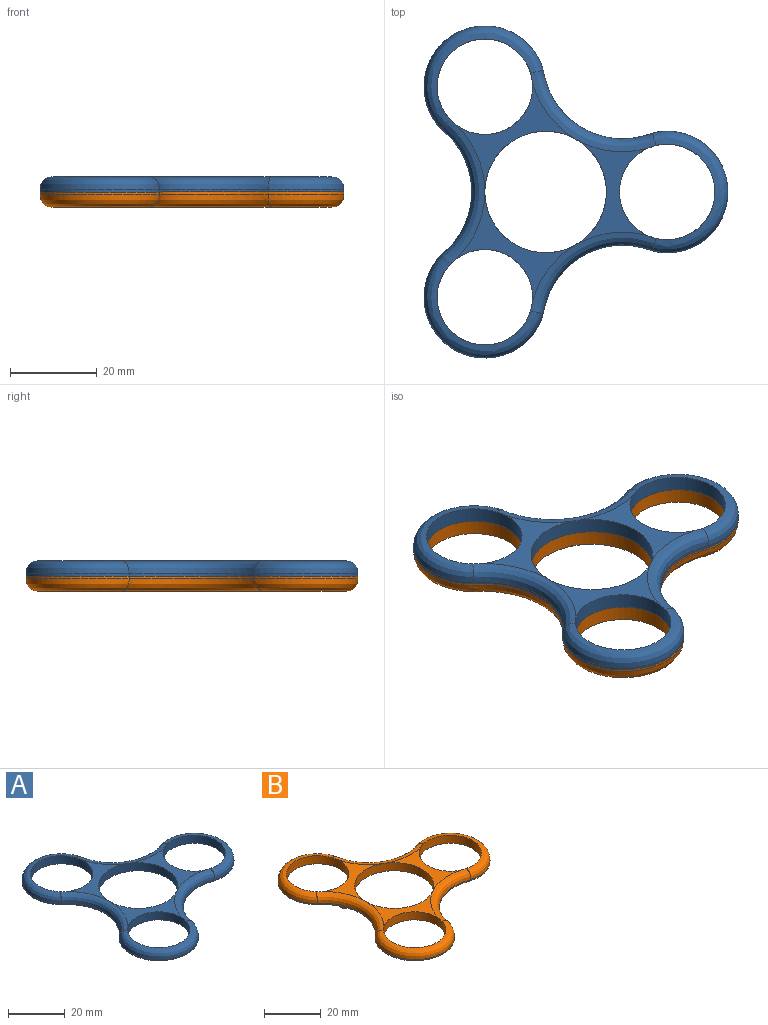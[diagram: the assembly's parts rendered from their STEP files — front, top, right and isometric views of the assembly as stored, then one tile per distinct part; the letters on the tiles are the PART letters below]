
ASSEMBLY  parts=2 mates=1
PART A: 32 faces, bbox 70.2x76.6x3.5 mm
  f0: plane 27.54x25.49mm, normal (0,0,1), area 113.9mm2, adj f7,f9,f16,f19
  f1: plane 24.28x16.61mm, normal (0,0,1), area 114mm2, adj f7,f10,f15,f19
  f2: cylinder r=18.43mm len=25.08mm, axis (0,0,-1), area 16.7mm2, adj f3,f11,f13,f15
  f3: cylinder r=14mm len=27.47mm, axis (0,0,-1), area 25.5mm2, adj f2,f4,f13,f14
  f4: cylinder r=18.43mm len=28.96mm, axis (0,0,-1), area 16.7mm2, adj f3,f5,f13,f16
  f5: cylinder r=14mm len=27.47mm, axis (0,0,-1), area 25.5mm2, adj f4,f6,f13,f18
  f6: cylinder r=18.43mm len=25.08mm, axis (0,0,-1), area 16.7mm2, adj f5,f11,f13,f19
  f7: cylinder r=14mm len=28mm, axis (0,0,-1), area 307.9mm2, adj f0,f1,f12,f13
  f8: cylinder r=11mm len=22mm, axis (0,0,-1), area 241.9mm2, adj f12,f13,f14,f15,f16
  f9: cylinder r=11mm len=22mm, axis (0,0,-1), area 241.9mm2, adj f0,f13,f16,f18,f19
  f10: cylinder r=11mm len=22mm, axis (0,0,-1), area 241.9mm2, adj f1,f13,f15,f17,f19
  f11: cylinder r=14mm len=28mm, axis (0,0,-1), area 25.5mm2, adj f2,f6,f13,f17
  f12: plane 27.54x25.49mm, normal (0,0,1), area 113.9mm2, adj f7,f8,f15,f16
  f13: plane 76.5x70mm, normal (0,0,-1), area 1029.2mm2, adj f2,f3,f4,f5,f6,f7,f8,f9
  f14: bspline ~27.47x23.76mm, area 228.9mm2, adj f3,f8,f15,f16
  f15: bspline ~31.12x20.64mm, area 170.3mm2, adj f1,f2,f8,f10,f12,f14,f17
  f16: bspline ~35.93x11.38mm, area 170.3mm2, adj f0,f4,f8,f9,f12,f14,f18
  f17: bspline ~27.99x17.43mm, area 228.9mm2, adj f10,f11,f15,f19
  f18: bspline ~28.1x25.54mm, area 228.9mm2, adj f5,f9,f16,f19
  f19: bspline ~29.17x18.8mm, area 170.3mm2, adj f0,f1,f6,f9,f10,f17,f18
  f20: cylinder r=1.5mm len=3mm, axis (0,0,-1), area 18.8mm2, adj f13,f21
  f21: plane 3x3mm, normal (0,0,-1), area 7.1mm2, adj f20
  f22: cylinder r=1.5mm len=3mm, axis (0,0,-1), area 18.8mm2, adj f13,f23
  f23: plane 3x3mm, normal (0,0,-1), area 7.1mm2, adj f22
  f24: cylinder r=1.5mm len=3mm, axis (0,0,-1), area 18.8mm2, adj f13,f25
  f25: plane 3x3mm, normal (0,0,-1), area 7.1mm2, adj f24
  f26: cylinder r=1.5mm len=3mm, axis (0,0,-1), area 18.8mm2, adj f13,f27
  f27: plane 3x3mm, normal (0,0,-1), area 7.1mm2, adj f26
  f28: cylinder r=1.5mm len=3mm, axis (0,0,-1), area 18.8mm2, adj f13,f29
  f29: plane 3x3mm, normal (0,0,-1), area 7.1mm2, adj f28
  f30: cylinder r=1.5mm len=3mm, axis (0,0,-1), area 18.8mm2, adj f13,f31
  f31: plane 3x3mm, normal (0,0,-1), area 7.1mm2, adj f30
PART B: 32 faces, bbox 70.2x76.6x5.5 mm
  f0: plane 27.54x25.49mm, normal (0,0,1), area 113.9mm2, adj f7,f9,f16,f19
  f1: plane 24.28x16.61mm, normal (0,0,1), area 114mm2, adj f7,f10,f15,f19
  f2: cylinder r=18.43mm len=25.08mm, axis (0,0,-1), area 16.7mm2, adj f3,f11,f13,f15
  f3: cylinder r=14mm len=27.47mm, axis (0,0,-1), area 25.5mm2, adj f2,f4,f13,f14
  f4: cylinder r=18.43mm len=28.96mm, axis (0,0,-1), area 16.7mm2, adj f3,f5,f13,f16
  f5: cylinder r=14mm len=27.47mm, axis (0,0,-1), area 25.5mm2, adj f4,f6,f13,f18
  f6: cylinder r=18.43mm len=25.08mm, axis (0,0,-1), area 16.7mm2, adj f5,f11,f13,f19
  f7: cylinder r=14mm len=28mm, axis (0,0,-1), area 307.9mm2, adj f0,f1,f12,f13
  f8: cylinder r=11mm len=22mm, axis (0,0,-1), area 241.9mm2, adj f12,f13,f14,f15,f16
  f9: cylinder r=11mm len=22mm, axis (0,0,-1), area 241.9mm2, adj f0,f13,f16,f18,f19
  f10: cylinder r=11mm len=22mm, axis (0,0,-1), area 241.9mm2, adj f1,f13,f15,f17,f19
  f11: cylinder r=14mm len=28mm, axis (0,0,-1), area 25.5mm2, adj f2,f6,f13,f17
  f12: plane 27.54x25.49mm, normal (0,0,1), area 113.9mm2, adj f7,f8,f15,f16
  f13: plane 76.5x70mm, normal (0,0,-1), area 1029.2mm2, adj f2,f3,f4,f5,f6,f7,f8,f9
  f14: bspline ~27.47x23.76mm, area 228.9mm2, adj f3,f8,f15,f16
  f15: bspline ~31.12x20.64mm, area 170.3mm2, adj f1,f2,f8,f10,f12,f14,f17
  f16: bspline ~35.93x11.38mm, area 170.3mm2, adj f0,f4,f8,f9,f12,f14,f18
  f17: bspline ~27.99x17.43mm, area 228.9mm2, adj f10,f11,f15,f19
  f18: bspline ~28.1x25.54mm, area 228.9mm2, adj f5,f9,f16,f19
  f19: bspline ~29.17x18.8mm, area 170.3mm2, adj f0,f1,f6,f9,f10,f17,f18
  f20: cylinder r=1.5mm len=3mm, axis (0,0,1), area 18.8mm2, adj f13,f21
  f21: plane 3x3mm, normal (0,0,-1), area 7.1mm2, adj f20
  f22: cylinder r=1.5mm len=3mm, axis (0,0,1), area 18.8mm2, adj f13,f23
  f23: plane 3x3mm, normal (0,0,-1), area 7.1mm2, adj f22
  f24: cylinder r=1.5mm len=3mm, axis (0,0,1), area 18.8mm2, adj f13,f25
  f25: plane 3x3mm, normal (0,0,-1), area 7.1mm2, adj f24
  f26: cylinder r=1.5mm len=3mm, axis (0,0,1), area 18.8mm2, adj f13,f27
  f27: plane 3x3mm, normal (0,0,-1), area 7.1mm2, adj f26
  f28: cylinder r=1.5mm len=3mm, axis (0,0,1), area 18.8mm2, adj f13,f29
  f29: plane 3x3mm, normal (0,0,-1), area 7.1mm2, adj f28
  f30: cylinder r=1.5mm len=3mm, axis (0,0,1), area 18.8mm2, adj f13,f31
  f31: plane 3x3mm, normal (0,0,-1), area 7.1mm2, adj f30
PLACE A t=(-11.26,30.19,-19.45)mm
PLACE B rot(axis=(1,0,0),180deg) t=(-11.26,30.19,-19.45)mm
MATE slider B.f7 <-> A.f7  axis (0,0,1) through (-11.26,30.19,-19.45)mm
